# Revit family: Chair-Evolve-2-Allermuir-Task_Seating
name_source: partatom
category: Furniture
revit_build: Autodesk Revit Architecture 2012 (Build: 20110309_2315(x64)
units: mm (PartAtom-declared; Revit-internal decimal feet)

## types (6) — shared parameters
04 CSI = 12 51 00
2.5" Casters = Yes
95 CSI = 12510
Advanced Sync Tilt with Multi Position Back = Yes
Arm Height = 67 1/2"
Arm Height Range = 6.75" - 10.75"
Assembly Code = E2020200
Base or Frame = YES
Black Components = Yes
Black GRP Base = Yes
Black Gas Lift = Yes
CAD Blocks = http://www.allermuir.net
Height Adjustable Arms with Multi funtction Pad = No
Height Range = 42" - 47.5"
Injection molded, contoured back panel in Black Plastic and upholstered seat = Yes
LEED Stats = http://www.allermuir.net
Lumbar Adjustment = Yes
Manufacturer = Allermuir
Manufacturer Fax = (419) 887 5805
Negative Seat Tilt = Yes
Overall Depth = 25 1/2"
Overall Height = 42"
Pedestal Base = YES
Polished Aluminum Base = No
Pricing URL = http://www.allermuir.net
Product Line = Evolve
Product Page URL = http://www.allermuir.net
Seat Depth = 18 1/2"
Seat Depth Adjustment = Yes
Seat Height = 18 1/2"
Seat Height Range = 18.5" - 23.25"
Seat Width = 20"
Specifications URL = http://www.allermuir.net
Stacks = No
Subcategory = Task Seating
Swaged Tubular Steel Legs = NO
Task Seating Brochure URL = http://www.allermuir.net
URL = http://www.allermuir.net
Upholstered Seat = YES
ecoScorecard_data = http://thesenatorgroup.ecoscorecard.com

http://thesenatorgroup.ecoscorecard.com

http://thesenatorgroup.ecoscorecard.com

http://thesenatorgroup.ecoscorecard.com

## per-type parameters (varying)
| type | Airflow Back Mesh | Black Plastic Back Membrane | Description | Height Adjustable Arms | Membrane Visibility | Overall Width | Plastic Arms in Black | Plugin Data URL | Polished Aluminum Arm Carrier | Slimline Upholstery | Two Tone Upholstery | Upholstered Back | Weight | White Plastic Back Membrane |
| EV2640 | No | No | Upholstered search & back, no arms | No | Yes | 20" | NO | http://thesenatorgroup.ecoscorecard.com | No | Yes | Yes | YES | 37.00 lb | No |
| EV2640HA | No | No | Upholstered search & back, with height adjustable arms | Yes | No | 27 1/2" | YES | http://products.ecoscorecard.com | Yes | Yes | Yes | YES | 39.00 lb | No |
| EV2740 | Yes | Yes | Membrane back, no arms | No | No | 20" | NO | http://products.ecoscorecard.com | No | No | No | NO | 35.00 lb | Yes |
| EV2740HA | Yes | Yes | Membrane back, with height adjustable arms | Yes | No | 27 1/2" | YES | http://products.ecoscorecard.com | Yes | No | No | NO | 37.00 lb | Yes |
| EV2740MF | Yes | Yes | Membrane back, with multi-function arms | Yes | No | 27 1/2" | YES | http://products.ecoscorecard.com | Yes | No | No | NO | 37.00 lb | Yes |
| EV2640MF | No | No | Upholstered search & back, with height adjustable arms | Yes | No | 27 1/2" | YES | http://products.ecoscorecard.com | Yes | Yes | Yes | YES | 39.00 lb | No |

note: column(s) folded — value = type name in every type: Model

## geometry (parser evidence)
native form markers: Blend x4, Sweep x14
no freeform markers — native parametric forms only
